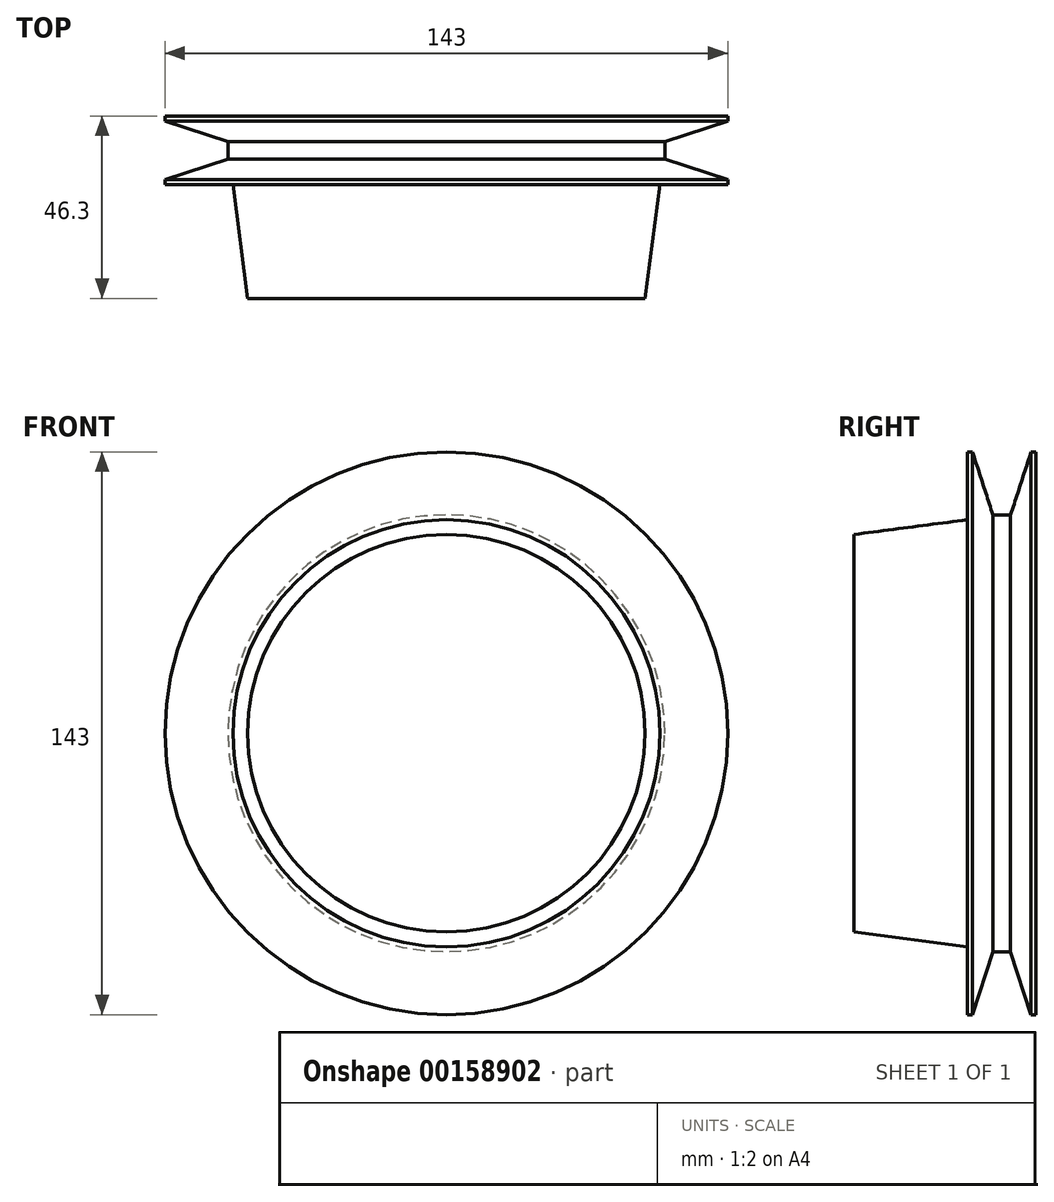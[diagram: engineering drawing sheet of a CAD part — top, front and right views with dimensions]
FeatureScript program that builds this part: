
annotation { "Feature Type Name" : "Feature", "Feature Type Description" : "" }
export const myFeature = defineFeature(function(context is Context, id is Id, definition is map)
    precondition{}
    {
        {
            var Q0;
            Q0=qCreatedBy(makeId("Right.planeOp"),FACE);
            var sketch = newSketch(context, id + "F0", { "sketchPlane" : qUnion([Q0])});
            skLineSegment(sketch, "E0", {"start": v(0, 0) * mm, "end": v(0, 50.5) * mm});
            skLineSegment(sketch, "E1", {"start": v(0, 50.5) * mm, "end": v(28.9, 54.25) * mm});
            skLineSegment(sketch, "E2", {"start": v(28.9, 54.25) * mm, "end": v(28.9, 71.5) * mm});
            skLineSegment(sketch, "E3", {"start": v(28.9, 71.5) * mm, "end": v(30.15, 71.5) * mm});
            skLineSegment(sketch, "E4", {"start": v(30.15, 71.5) * mm, "end": v(35.35, 55.5) * mm});
            skLineSegment(sketch, "E5", {"start": v(35.35, 55.5) * mm, "end": v(39.85, 55.5) * mm});
            skLineSegment(sketch, "E6", {"start": v(39.85, 55.5) * mm, "end": v(45.05, 71.5) * mm});
            skLineSegment(sketch, "E7", {"start": v(45.05, 71.5) * mm, "end": v(46.3, 71.5) * mm});
            skLineSegment(sketch, "E8", {"start": v(46.3, 71.5) * mm, "end": v(46.3, 0) * mm});
            skLineSegment(sketch, "E9", {"start": v(46.3, 0) * mm, "end": v(0, 0) * mm});
            skLineSegment(sketch, "E10", {"start": v(0, 0) * mm, "end": v(-64.43, 0) * mm, "construction": true});
            skSolve(sketch);
        }
        {
            var Q0;
            Q0 = qSketchRegion(id + "F0", true);
            var Q1;
            Q1=sQuery(id+"F0.wireOp",EDGE,"E10");
            revolve(context, id + "F1", {"entities" : qUnion([Q0]), "axis" : qUnion([Q1]), "revolveType" : RevolveType.FULL});
        }
    });
